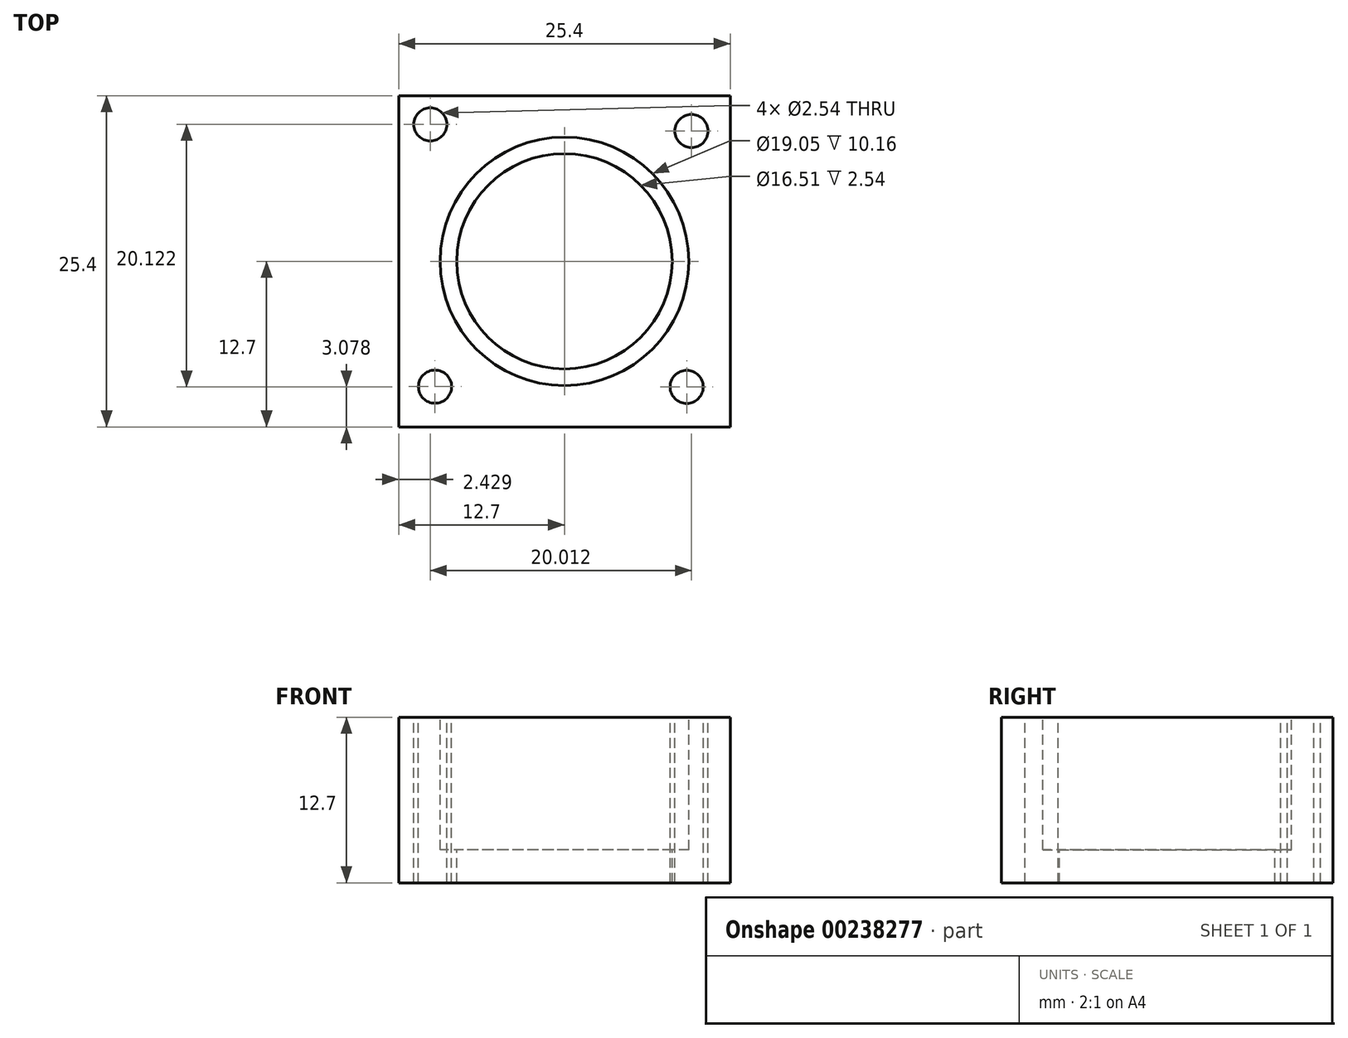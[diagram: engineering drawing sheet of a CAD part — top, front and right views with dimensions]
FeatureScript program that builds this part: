
annotation { "Feature Type Name" : "Feature", "Feature Type Description" : "" }
export const myFeature = defineFeature(function(context is Context, id is Id, definition is map)
    precondition{}
    {
        {
            var Q0;
            Q0=qCreatedBy(makeId("Top.planeOp"),FACE);
            var sketch = newSketch(context, id + "F0", { "sketchPlane" : qUnion([Q0])});
            skLineSegment(sketch, "E0.bottom", {"start": v(0, 0) * mm, "end": v(25.4, 0) * mm});
            skLineSegment(sketch, "E0.top", {"start": v(0, 25.4) * mm, "end": v(25.4, 25.4) * mm});
            skLineSegment(sketch, "E0.left", {"start": v(0, 0) * mm, "end": v(0, 25.4) * mm});
            skLineSegment(sketch, "E0.right", {"start": v(25.4, 0) * mm, "end": v(25.4, 25.4) * mm});
            skSolve(sketch);
        }
        {
            var Q0;
            Q0 = qSketchRegion(id + "F0", true);
            extrude(context, id + "F1", {"entities" : qUnion([Q0]), "depth" : 12.7 * mm});
        }
        {
            var Q0;
            Q0=makeQuery(id+"F1.opExtrude","CAP_FACE",FACE,{"disambiguationData":[OSD([sQuery(id+"F0.wireOp",EDGE,"E0.bottom"),sQuery(id+"F0.wireOp",EDGE,"E0.top"),sQuery(id+"F0.wireOp",EDGE,"E0.left"),sQuery(id+"F0.wireOp",EDGE,"E0.right")])],"isStart":false});
            var sketch = newSketch(context, id + "F2", { "sketchPlane" : qUnion([Q0])});
            skCircle(sketch, "E1", {"center": v(12.7, 12.7) * mm, "radius": 9.53 * mm});
            skPoint(sketch, "E1.centerSnap0", {"position": v(25.4, 12.7) * mm});
            skPoint(sketch, "E1.centerSnap1", {"position": v(12.7, 25.4) * mm});
            skSolve(sketch);
        }
        {
            var Q0;
            Q0=makeQuery(id+"F2.imprint","IMPRINT",FACE,{"disambiguationData":[TD([[makeQuery(id+"F2.imprint","IMPRINT",EDGE,{"derivedFrom":sQuery(id+"F2.wireOp",EDGE,"E1")}),1.0]])]});
            extrude(context, id + "F3", {"entities" : qUnion([Q0]), "operationType" : NewBodyOperationType.REMOVE, "oppositeDirection" : true, "depth" : 10.16 * mm});
        }
        {
            var Q0;
            Q0=makeQuery(id+"F3.boolean.opBoolean","COPY",FACE,{"derivedFrom":makeQuery(id+"F3.opExtrude","CAP_FACE",FACE,{"disambiguationData":[OSD([sQuery(id+"F2.wireOp",EDGE,"E1")])],"isStart":false})});
            var sketch = newSketch(context, id + "F4", { "sketchPlane" : qUnion([Q0])});
            skCircle(sketch, "E2", {"center": v(12.7, 12.7) * mm, "radius": 8.26 * mm});
            skSolve(sketch);
        }
        {
            var Q0;
            Q0=makeQuery(id+"F4.imprint","IMPRINT",FACE,{"disambiguationData":[TD([[makeQuery(id+"F4.imprint","IMPRINT",EDGE,{"derivedFrom":sQuery(id+"F4.wireOp",EDGE,"E2")}),1.0]])]});
            extrude(context, id + "F5", {"entities" : qUnion([Q0]), "operationType" : NewBodyOperationType.REMOVE, "endBound" : BoundingType.THROUGH_ALL, "oppositeDirection" : true, "depth" : 25.4 * mm});
        }
        {
            var Q0;
            Q0=makeQuery(id+"F1.opExtrude","CAP_FACE",FACE,{"disambiguationData":[OSD([sQuery(id+"F0.wireOp",EDGE,"E0.bottom"),sQuery(id+"F0.wireOp",EDGE,"E0.top"),sQuery(id+"F0.wireOp",EDGE,"E0.left"),sQuery(id+"F0.wireOp",EDGE,"E0.right")])],"isStart":false});
            var sketch = newSketch(context, id + "F6", { "sketchPlane" : qUnion([Q0])});
            skCircle(sketch, "E3", {"center": v(2.79, 3.1) * mm, "radius": 1.27 * mm});
            skSolve(sketch);
        }
        {
            var Q0;
            Q0 = qSketchRegion(id + "F6", true);
            extrude(context, id + "F7", {"entities" : qUnion([Q0]), "operationType" : NewBodyOperationType.REMOVE, "endBound" : BoundingType.THROUGH_ALL, "oppositeDirection" : true, "depth" : 25.4 * mm});
        }
        {
            var Q0;
            Q0=makeQuery(id+"F1.opExtrude","CAP_FACE",FACE,{"disambiguationData":[OSD([sQuery(id+"F0.wireOp",EDGE,"E0.bottom"),sQuery(id+"F0.wireOp",EDGE,"E0.top"),sQuery(id+"F0.wireOp",EDGE,"E0.left"),sQuery(id+"F0.wireOp",EDGE,"E0.right")])],"isStart":false});
            var sketch = newSketch(context, id + "F8", { "sketchPlane" : qUnion([Q0])});
            skCircle(sketch, "E4", {"center": v(2.43, 23.2) * mm, "radius": 1.27 * mm});
            skSolve(sketch);
        }
        {
            var Q0;
            Q0=makeQuery(id+"F8.imprint","IMPRINT",FACE,{"disambiguationData":[TD([[makeQuery(id+"F8.imprint","IMPRINT",EDGE,{"derivedFrom":sQuery(id+"F8.wireOp",EDGE,"E4")}),1.0]])]});
            var Q1;
            Q1=sQuery(id+"F8.wireOp",EDGE,"E4");
            extrude(context, id + "F9", {"entities" : qUnion([Q0]), "operationType" : NewBodyOperationType.REMOVE, "surfaceEntities" : qUnion([Q1]), "endBound" : BoundingType.THROUGH_ALL, "oppositeDirection" : true, "depth" : 25.4 * mm});
        }
        {
            var Q0;
            Q0=makeQuery(id+"F1.opExtrude","CAP_FACE",FACE,{"disambiguationData":[OSD([sQuery(id+"F0.wireOp",EDGE,"E0.bottom"),sQuery(id+"F0.wireOp",EDGE,"E0.top"),sQuery(id+"F0.wireOp",EDGE,"E0.left"),sQuery(id+"F0.wireOp",EDGE,"E0.right")])],"isStart":false});
            var sketch = newSketch(context, id + "F10", { "sketchPlane" : qUnion([Q0])});
            skCircle(sketch, "E5", {"center": v(22.07, 3.08) * mm, "radius": 1.27 * mm});
            skSolve(sketch);
        }
        {
            var Q0;
            Q0=makeQuery(id+"F10.imprint","IMPRINT",FACE,{"disambiguationData":[TD([[makeQuery(id+"F10.imprint","IMPRINT",EDGE,{"derivedFrom":sQuery(id+"F10.wireOp",EDGE,"E5")}),1.0]])]});
            var Q1;
            Q1=sQuery(id+"F10.wireOp",EDGE,"E5");
            extrude(context, id + "F11", {"entities" : qUnion([Q0]), "operationType" : NewBodyOperationType.REMOVE, "surfaceEntities" : qUnion([Q1]), "endBound" : BoundingType.THROUGH_ALL, "oppositeDirection" : true, "depth" : 25.4 * mm});
        }
        {
            var Q0;
            Q0=makeQuery(id+"F1.opExtrude","CAP_FACE",FACE,{"disambiguationData":[OSD([sQuery(id+"F0.wireOp",EDGE,"E0.bottom"),sQuery(id+"F0.wireOp",EDGE,"E0.top"),sQuery(id+"F0.wireOp",EDGE,"E0.left"),sQuery(id+"F0.wireOp",EDGE,"E0.right")])],"isStart":false});
            var sketch = newSketch(context, id + "F12", { "sketchPlane" : qUnion([Q0])});
            skCircle(sketch, "E6", {"center": v(22.44, 22.7) * mm, "radius": 1.27 * mm});
            skSolve(sketch);
        }
        {
            var Q0;
            Q0=makeQuery(id+"F12.imprint","IMPRINT",FACE,{"disambiguationData":[TD([[makeQuery(id+"F12.imprint","IMPRINT",EDGE,{"derivedFrom":sQuery(id+"F12.wireOp",EDGE,"E6")}),1.0]])]});
            extrude(context, id + "F13", {"entities" : qUnion([Q0]), "operationType" : NewBodyOperationType.REMOVE, "endBound" : BoundingType.THROUGH_ALL, "oppositeDirection" : true, "depth" : 25.4 * mm});
        }
    });
